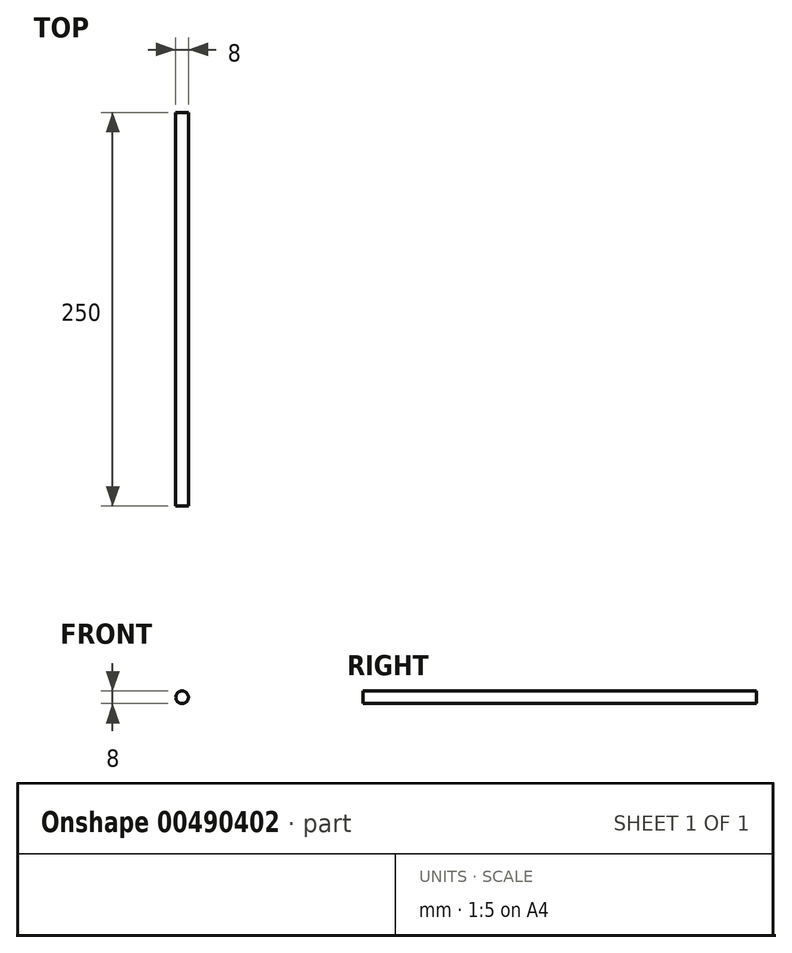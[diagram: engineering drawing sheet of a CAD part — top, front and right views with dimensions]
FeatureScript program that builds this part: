
annotation { "Feature Type Name" : "Feature", "Feature Type Description" : "" }
export const myFeature = defineFeature(function(context is Context, id is Id, definition is map)
    precondition{}
    {
        {
            var Q0;
            Q0=qCreatedBy(makeId("Front.planeOp"),FACE);
            var sketch = newSketch(context, id + "F0", { "sketchPlane" : qUnion([Q0])});
            skCircle(sketch, "E0", {"center": v(0, 0) * mm, "radius": 4 * mm});
            skSolve(sketch);
        }
        {
            var Q0;
            Q0=makeQuery(id+"F0.imprint","IMPRINT",FACE,{"disambiguationData":[TD([[makeQuery(id+"F0.imprint","IMPRINT",EDGE,{"derivedFrom":sQuery(id+"F0.wireOp",EDGE,"E0")}),1.0]])]});
            extrude(context, id + "F1", {"entities" : qUnion([Q0]), "depth" : 250 * mm});
        }
    });
